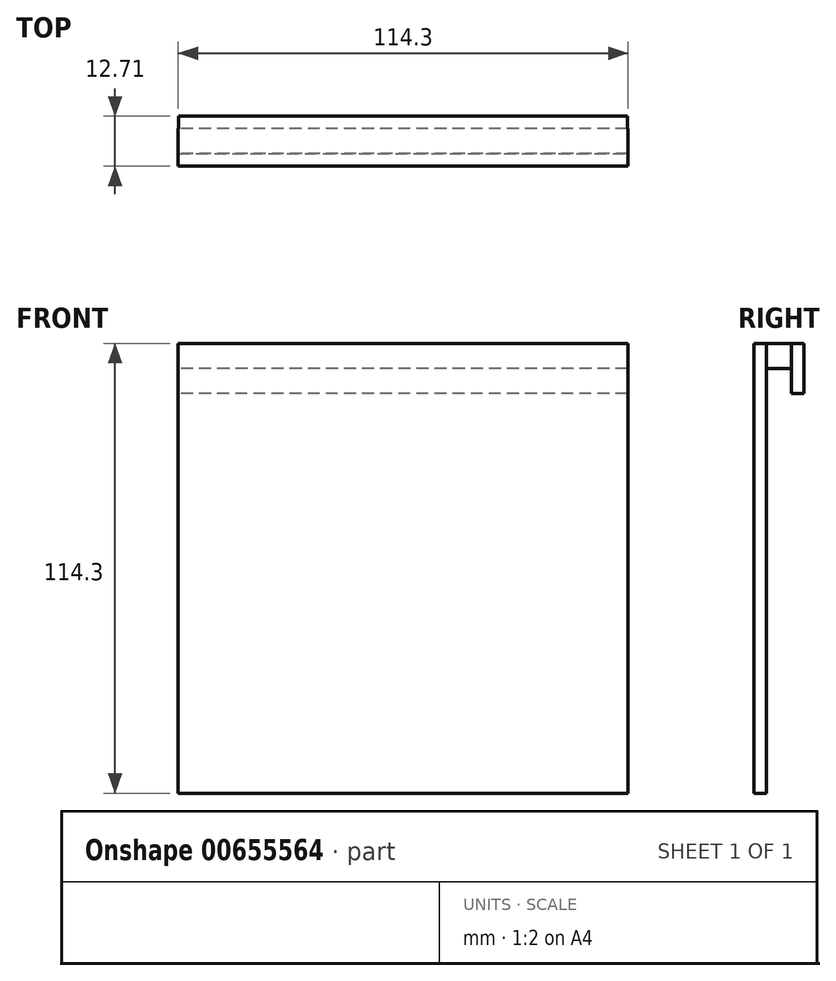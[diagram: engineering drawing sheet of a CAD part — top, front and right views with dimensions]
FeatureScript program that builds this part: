
annotation { "Feature Type Name" : "Feature", "Feature Type Description" : "" }
export const myFeature = defineFeature(function(context is Context, id is Id, definition is map)
    precondition{}
    {
        {
            var Q0;
            Q0=qCreatedBy(makeId("Front.planeOp"),FACE);
            var sketch = newSketch(context, id + "F0", { "sketchPlane" : qUnion([Q0])});
            skLineSegment(sketch, "E0.bottom", {"start": v(-57.49, 55.26) * mm, "end": v(56.81, 55.26) * mm});
            skLineSegment(sketch, "E0.top", {"start": v(-57.49, -59.04) * mm, "end": v(56.81, -59.04) * mm});
            skLineSegment(sketch, "E0.left", {"start": v(-57.49, 55.26) * mm, "end": v(-57.49, -59.04) * mm});
            skLineSegment(sketch, "E0.right", {"start": v(56.81, 55.26) * mm, "end": v(56.81, -59.04) * mm});
            skSolve(sketch);
        }
        {
            var Q0;
            Q0=qCreatedBy(makeId("Right.planeOp"),FACE);
            var sketch = newSketch(context, id + "F1", { "sketchPlane" : qUnion([Q0])});
            skLineSegment(sketch, "E1.bottom", {"start": v(0, 55.25) * mm, "end": v(6.35, 55.25) * mm});
            skLineSegment(sketch, "E1.top", {"start": v(0, 48.9) * mm, "end": v(6.35, 48.9) * mm});
            skLineSegment(sketch, "E1.left", {"start": v(0, 55.25) * mm, "end": v(0, 48.9) * mm});
            skLineSegment(sketch, "E1.right", {"start": v(6.35, 55.25) * mm, "end": v(6.35, 48.9) * mm});
            skLineSegment(sketch, "E2.bottom", {"start": v(6.35, 55.25) * mm, "end": v(9.53, 55.25) * mm});
            skLineSegment(sketch, "E2.top", {"start": v(6.35, 42.55) * mm, "end": v(9.53, 42.55) * mm});
            skLineSegment(sketch, "E2.left", {"start": v(6.35, 55.25) * mm, "end": v(6.35, 42.55) * mm});
            skLineSegment(sketch, "E2.right", {"start": v(9.53, 55.25) * mm, "end": v(9.53, 42.55) * mm});
            skSolve(sketch);
        }
        {
            var Q0;
            Q0 = qSketchRegion(id + "F0", true);
            extrude(context, id + "F2", {"entities" : qUnion([Q0]), "depth" : 3.17 * mm, "offsetDistance" : 25.4 * mm});
        }
        {
            var Q0;
            {var subQ0=sQuery(id+"F1.wireOp",EDGE,"E1.bottom");Q0=makeQuery(id+"F1.imprint","IMPRINT",FACE,{"disambiguationData":[TD([[makeQuery(id+"F1.imprint","IMPRINT",EDGE,{"derivedFrom":subQ0}),-1.0]])]});}
            extrude(context, id + "F3", {"entities" : qUnion([Q0]), "operationType" : NewBodyOperationType.ADD, "depth" : 56.72 * mm, "offsetDistance" : 25.4 * mm});
        }
        {
            var Q0;
            Q0=makeQuery(id+"F3.opExtrude","CAP_FACE",FACE,{"disambiguationData":[OSD([sQuery(id+"F1.wireOp",EDGE,"E1.bottom"),sQuery(id+"F1.wireOp",EDGE,"E1.top"),sQuery(id+"F1.wireOp",EDGE,"E1.left"),sQuery(id+"F1.wireOp",EDGE,"E2.left")])],"isStart":true});
            extrude(context, id + "F4", {"entities" : qUnion([Q0]), "operationType" : NewBodyOperationType.ADD, "depth" : 57.48 * mm, "offsetDistance" : 25.4 * mm});
        }
        {
            var Q0;
            Q0 = qSketchRegion(id + "F1", true);
            extrude(context, id + "F5", {"entities" : qUnion([Q0]), "operationType" : NewBodyOperationType.ADD, "depth" : 56.64 * mm, "offsetDistance" : 25.4 * mm});
        }
        {
            var Q0;
            Q0=makeQuery(id+"F5.opExtrude","CAP_FACE",FACE,{"disambiguationData":[OSD([sQuery(id+"F1.wireOp",EDGE,"E1.bottom"),sQuery(id+"F1.wireOp",EDGE,"E1.top"),sQuery(id+"F1.wireOp",EDGE,"E1.left"),sQuery(id+"F1.wireOp",EDGE,"E2.bottom"),sQuery(id+"F1.wireOp",EDGE,"E2.top"),sQuery(id+"F1.wireOp",EDGE,"E2.left"),sQuery(id+"F1.wireOp",EDGE,"E2.right")])],"isStart":true});
            extrude(context, id + "F6", {"entities" : qUnion([Q0]), "operationType" : NewBodyOperationType.ADD, "depth" : 57.43 * mm, "offsetDistance" : 25.4 * mm});
        }
    });
